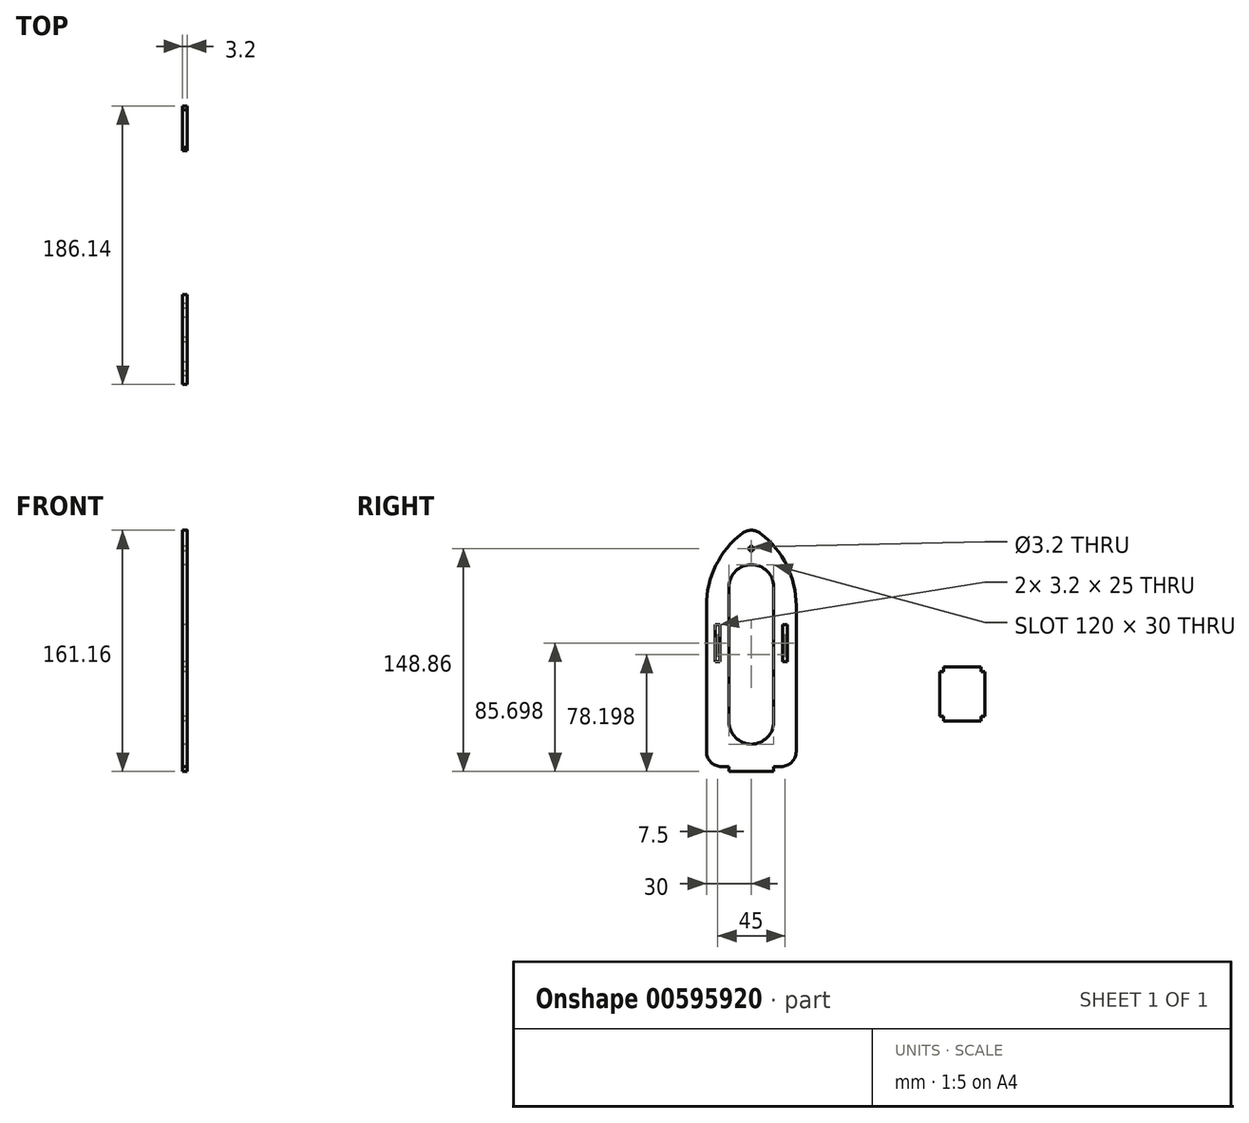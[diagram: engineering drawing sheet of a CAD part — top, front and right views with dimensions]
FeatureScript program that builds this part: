
annotation { "Feature Type Name" : "Feature", "Feature Type Description" : "" }
export const myFeature = defineFeature(function(context is Context, id is Id, definition is map)
    precondition{}
    {
        {
            var Q0;
            Q0=qCreatedBy(makeId("Right.planeOp"),FACE);
            var sketch = newSketch(context, id + "F0", { "sketchPlane" : qUnion([Q0])});
            skLineSegment(sketch, "E0.bottom", {"start": v(-20.9, 116.5) * mm, "end": v(-20.9, 116.5) * mm});
            skLineSegment(sketch, "E0.top", {"start": v(-50.9, -33.5) * mm, "end": v(-35.9, -33.5) * mm});
            skLineSegment(sketch, "E0.left", {"start": v(-50.9, 73.97) * mm, "end": v(-50.9, -33.5) * mm});
            skLineSegment(sketch, "E0.right", {"start": v(9.1, 73.97) * mm, "end": v(9.1, -33.5) * mm});
            skLineSegment(sketch, "E1.bottom", {"start": v(-20.9, 101.5) * mm, "end": v(-20.9, 101.5) * mm});
            skLineSegment(sketch, "E1.top", {"start": v(-20.9, -18.5) * mm, "end": v(-20.9, -18.5) * mm});
            skLineSegment(sketch, "E1.left", {"start": v(-35.9, 86.5) * mm, "end": v(-35.9, -3.5) * mm});
            skLineSegment(sketch, "E1.right", {"start": v(-5.9, 86.5) * mm, "end": v(-5.9, -3.5) * mm});
            skPoint(sketch, "E2.visualSharp", {"position": v(-50.9, 116.5) * mm});
            skPoint(sketch, "E3.visualSharp", {"position": v(9.1, 116.5) * mm});
            skPoint(sketch, "E4.visualSharp", {"position": v(-50.9, -33.5) * mm});
            skLineSegment(sketch, "E4.filletArc", {"start": v(-50.9, -33.5) * mm, "end": v(-50.9, -33.5) * mm});
            skPoint(sketch, "E5.visualSharp", {"position": v(9.1, -33.5) * mm});
            skLineSegment(sketch, "E5.filletArc", {"start": v(9.1, -33.5) * mm, "end": v(9.1, -33.5) * mm});
            skPoint(sketch, "E6.visualSharp", {"position": v(-35.9, 101.5) * mm});
            skArc(sketch, "E6.filletArc", {"start": v(-20.9, 101.5) * mm, "mid": v(-31.5, 97.1) * mm, "end": v(-35.9, 86.5) * mm});
            skPoint(sketch, "E7.visualSharp", {"position": v(-5.9, 101.5) * mm});
            skArc(sketch, "E7.filletArc", {"start": v(-5.9, 86.5) * mm, "mid": v(-10.3, 97.1) * mm, "end": v(-20.9, 101.5) * mm});
            skPoint(sketch, "E8.visualSharp", {"position": v(-5.9, -18.5) * mm});
            skArc(sketch, "E8.filletArc", {"start": v(-20.9, -18.5) * mm, "mid": v(-10.3, -14.1) * mm, "end": v(-5.9, -3.5) * mm});
            skPoint(sketch, "E9.visualSharp", {"position": v(-35.9, -18.5) * mm});
            skArc(sketch, "E9.filletArc", {"start": v(-35.9, -3.5) * mm, "mid": v(-31.5, -14.1) * mm, "end": v(-20.9, -18.5) * mm});
            skArc(sketch, "E10", {"start": v(9.1, 73.97) * mm, "mid": v(2.8, 100.98) * mm, "end": v(-14.82, 122.4) * mm});
            skArc(sketch, "E11", {"start": v(-26.98, 122.4) * mm, "mid": v(-44.6, 100.98) * mm, "end": v(-50.9, 73.97) * mm});
            skPoint(sketch, "E12.visualSharp", {"position": v(-20.9, 126.5) * mm});
            skArc(sketch, "E12.filletArc", {"start": v(-14.82, 122.4) * mm, "mid": v(-20.9, 124.46) * mm, "end": v(-26.98, 122.4) * mm});
            skCircle(sketch, "E13", {"center": v(-20.9, 112.16) * mm, "radius": 1.6 * mm});
            skLineSegment(sketch, "E14", {"start": v(-35.9, -33.5) * mm, "end": v(-35.9, -36.7) * mm});
            skLineSegment(sketch, "E15", {"start": v(-35.9, -36.7) * mm, "end": v(-5.9, -36.7) * mm});
            skLineSegment(sketch, "E16", {"start": v(-5.9, -36.7) * mm, "end": v(-5.9, -33.5) * mm});
            skLineSegment(sketch, "E17.trimOffspring", {"start": v(-5.9, -33.5) * mm, "end": v(9.1, -33.5) * mm});
            skLineSegment(sketch, "E18.bottom", {"start": v(0, 61.5) * mm, "end": v(3.2, 61.5) * mm});
            skLineSegment(sketch, "E18.top", {"start": v(0, 36.5) * mm, "end": v(3.2, 36.5) * mm});
            skLineSegment(sketch, "E18.left", {"start": v(0, 61.5) * mm, "end": v(0, 36.5) * mm});
            skLineSegment(sketch, "E18.right", {"start": v(3.2, 61.5) * mm, "end": v(3.2, 36.5) * mm});
            skLineSegment(sketch, "E19.bottom", {"start": v(-45, 61.5) * mm, "end": v(-41.8, 61.5) * mm});
            skLineSegment(sketch, "E19.top", {"start": v(-45, 36.5) * mm, "end": v(-41.8, 36.5) * mm});
            skLineSegment(sketch, "E19.left", {"start": v(-45, 61.5) * mm, "end": v(-45, 36.5) * mm});
            skLineSegment(sketch, "E19.right", {"start": v(-41.8, 61.5) * mm, "end": v(-41.8, 36.5) * mm});
            skLineSegment(sketch, "E20.bottom", {"start": v(105.24, 30) * mm, "end": v(107.74, 30) * mm});
            skLineSegment(sketch, "E20.top", {"start": v(105.24, 0) * mm, "end": v(107.74, 0) * mm});
            skLineSegment(sketch, "E20.left", {"start": v(105.24, 30) * mm, "end": v(105.24, 0) * mm});
            skLineSegment(sketch, "E20.right", {"start": v(135.24, 30) * mm, "end": v(135.24, 0) * mm});
            skLineSegment(sketch, "E21", {"start": v(107.74, 30) * mm, "end": v(107.74, 33.2) * mm});
            skLineSegment(sketch, "E22", {"start": v(107.74, 33.2) * mm, "end": v(132.74, 33.2) * mm});
            skLineSegment(sketch, "E23", {"start": v(132.74, 33.2) * mm, "end": v(132.74, 30) * mm});
            skLineSegment(sketch, "E24", {"start": v(132.74, 0) * mm, "end": v(132.74, -3.2) * mm});
            skLineSegment(sketch, "E25", {"start": v(132.74, -3.2) * mm, "end": v(107.74, -3.2) * mm});
            skLineSegment(sketch, "E26", {"start": v(107.74, -3.2) * mm, "end": v(107.74, 0) * mm});
            skLineSegment(sketch, "E27.trimOffspring", {"start": v(132.74, 30) * mm, "end": v(135.24, 30) * mm});
            skLineSegment(sketch, "E28.trimOffspring", {"start": v(132.74, 0) * mm, "end": v(135.24, 0) * mm});
            skSolve(sketch);
        }
        {
            var Q0;
            Q0=qSketchRegion(id+"F0",true);
            extrude(context, id + "F1", {"entities" : qUnion([Q0]), "depth" : 3.2 * mm, "offsetDistance" : 25 * mm});
        }
        {
            var Q0;
            Q0=makeQuery(id+"F1.opExtrude","SWEPT_EDGE",EDGE,{"disambiguationData":[OSD([sQuery(id+"F0.wireOp",EDGE,"E0.top"),sQuery(id+"F0.wireOp",EDGE,"E0.left")])]});
            var Q1;
            Q1=makeQuery(id+"F1.opExtrude","SWEPT_EDGE",EDGE,{"disambiguationData":[OSD([sQuery(id+"F0.wireOp",EDGE,"E0.right"),sQuery(id+"F0.wireOp",EDGE,"E17.trimOffspring")])]});
            fillet(context, id + "F2", {"entities" : qUnion([Q0, Q1]), "radius" : 10 * mm, "tangentPropagation" : true, "allowEdgeOverflow" : false});
        }
    });
